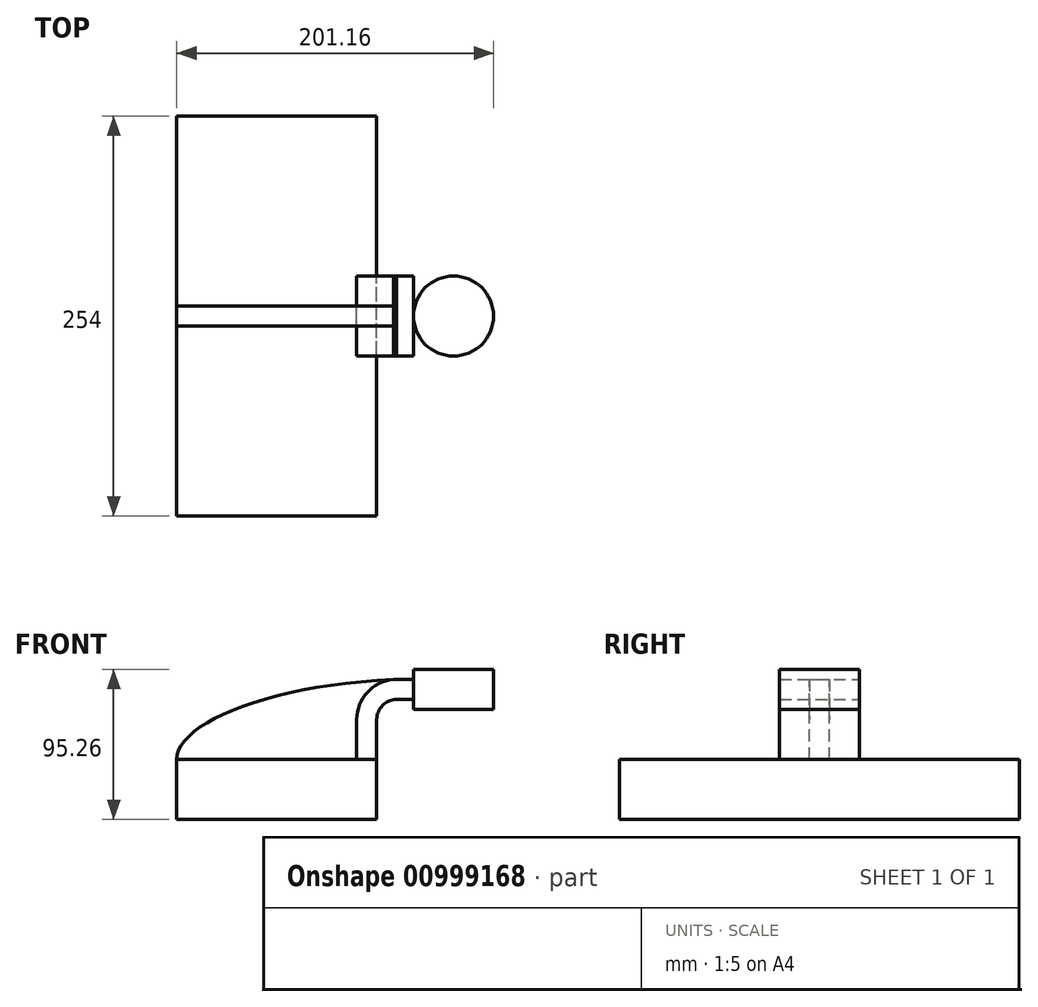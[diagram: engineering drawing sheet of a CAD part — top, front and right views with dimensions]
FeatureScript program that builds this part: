
annotation { "Feature Type Name" : "Feature", "Feature Type Description" : "" }
export const myFeature = defineFeature(function(context is Context, id is Id, definition is map)
    precondition{}
    {
        {
            var Q0;
            Q0=qCreatedBy(makeId("Front.planeOp"),FACE);
            var sketch = newSketch(context, id + "F0", { "sketchPlane" : qUnion([Q0])});
            skLineSegment(sketch, "E0.bottom", {"start": v(-63.5, 19.05) * mm, "end": v(63.5, 19.05) * mm});
            skLineSegment(sketch, "E0.top", {"start": v(-63.5, -19.05) * mm, "end": v(63.5, -19.05) * mm});
            skLineSegment(sketch, "E0.left", {"start": v(-63.5, 19.05) * mm, "end": v(-63.5, -19.05) * mm});
            skLineSegment(sketch, "E0.right", {"start": v(63.5, 19.05) * mm, "end": v(63.5, -19.05) * mm});
            skPoint(sketch, "E0.middle", {"position": v(0, 0) * mm});
            skLineSegment(sketch, "E1.bottom", {"start": v(86.86, 50.81) * mm, "end": v(137.66, 50.81) * mm});
            skLineSegment(sketch, "E1.top", {"start": v(86.86, 76.21) * mm, "end": v(137.66, 76.21) * mm});
            skLineSegment(sketch, "E1.left", {"start": v(86.86, 50.81) * mm, "end": v(86.86, 76.21) * mm});
            skLineSegment(sketch, "E1.right", {"start": v(137.66, 50.81) * mm, "end": v(137.66, 76.21) * mm});
            skLineSegment(sketch, "E2", {"start": v(63.5, 19.05) * mm, "end": v(63.5, 44.45) * mm});
            skArc(sketch, "E3", {"start": v(63.5, 44.45) * mm, "mid": v(67.22, 53.43) * mm, "end": v(76.2, 57.15) * mm});
            skLineSegment(sketch, "E4", {"start": v(76.2, 57.15) * mm, "end": v(112.26, 57.15) * mm});
            skLineSegment(sketch, "E5.0", {"start": v(76.2, 69.85) * mm, "end": v(112.26, 69.85) * mm});
            skArc(sketch, "E5.1", {"start": v(50.8, 44.45) * mm, "mid": v(58.24, 62.41) * mm, "end": v(76.2, 69.85) * mm});
            skLineSegment(sketch, "E5.2", {"start": v(50.8, 19.05) * mm, "end": v(50.8, 44.45) * mm});
            skFitSpline(sketch, "E6", {"points": [v(-63.5, 19.05) * mm, v(76.2, 69.85) * mm], "startDerivative": vector(-0.36, 68.22) * mm, "endDerivative": vector(246.25, 9.48) * mm});
            skLineSegment(sketch, "E7", {"start": v(86.86, 69.85) * mm, "end": v(112.26, 69.85) * mm});
            skLineSegment(sketch, "E8", {"start": v(112.26, 76.21) * mm, "end": v(112.26, 50.81) * mm});
            skSolve(sketch);
        }
        {
            var Q0;
            Q0=makeQuery(id+"F0.imprint","IMPRINT",FACE,{"disambiguationData":[TD([[makeQuery(id+"F0.imprint","IMPRINT",EDGE,{"derivedFrom":sQuery(id+"F0.wireOp",EDGE,"E0.top")}),1.0]])]});
            extrude(context, id + "F1", {"entities" : qUnion([Q0]), "endBound" : BoundingType.SYMMETRIC, "depth" : 254 * mm, "offsetDistance" : 25.4 * mm});
        }
        {
            var Q0;
            {var subQ1=sQuery(id+"F0.wireOp",EDGE,"E2");Q0=makeQuery(id+"F0.imprint","IMPRINT",FACE,{"disambiguationData":[TD([[makeQuery(id+"F0.imprint","IMPRINT",EDGE,{"derivedFrom":subQ1}),1.0]])]});}
            var Q1;
            {var subQ0=sQuery(id+"F0.wireOp",EDGE,"E7");Q1=makeQuery(id+"F0.imprint","IMPRINT",FACE,{"disambiguationData":[TD([[makeQuery(id+"F0.imprint","IMPRINT",EDGE,{"derivedFrom":subQ0}),-1.0]])]});}
            extrude(context, id + "F2", {"entities" : qUnion([Q0, Q1]), "endBound" : BoundingType.SYMMETRIC, "depth" : 50.8 * mm, "offsetDistance" : 25.4 * mm});
        }
        {
            var Q0;
            {var subQ3=sQuery(id+"F0.wireOp",EDGE,"E5.2");Q0=makeQuery(id+"F0.imprint","IMPRINT",FACE,{"disambiguationData":[TD([[makeQuery(id+"F0.imprint","IMPRINT",EDGE,{"derivedFrom":subQ3}),1.0]])]});}
            extrude(context, id + "F3", {"entities" : qUnion([Q0]), "endBound" : BoundingType.SYMMETRIC, "depth" : 12.7 * mm, "offsetDistance" : 25.4 * mm});
        }
        {
            var Q0;
            {var subQ4=sQuery(id+"F0.wireOp",EDGE,"E1.right");Q0=makeQuery(id+"F0.imprint","IMPRINT",FACE,{"disambiguationData":[TD([[makeQuery(id+"F0.imprint","IMPRINT",EDGE,{"derivedFrom":subQ4}),1.0]])]});}
            var Q1;
            Q1=sQuery(id+"F0.wireOp",EDGE,"E8");
            revolve(context, id + "F4", {"operationType" : NewBodyOperationType.ADD, "surfaceOperationType" : NewSurfaceOperationType.NEW, "entities" : qUnion([Q0]), "axis" : qUnion([Q1]), "revolveType" : RevolveType.FULL});
        }
    });
